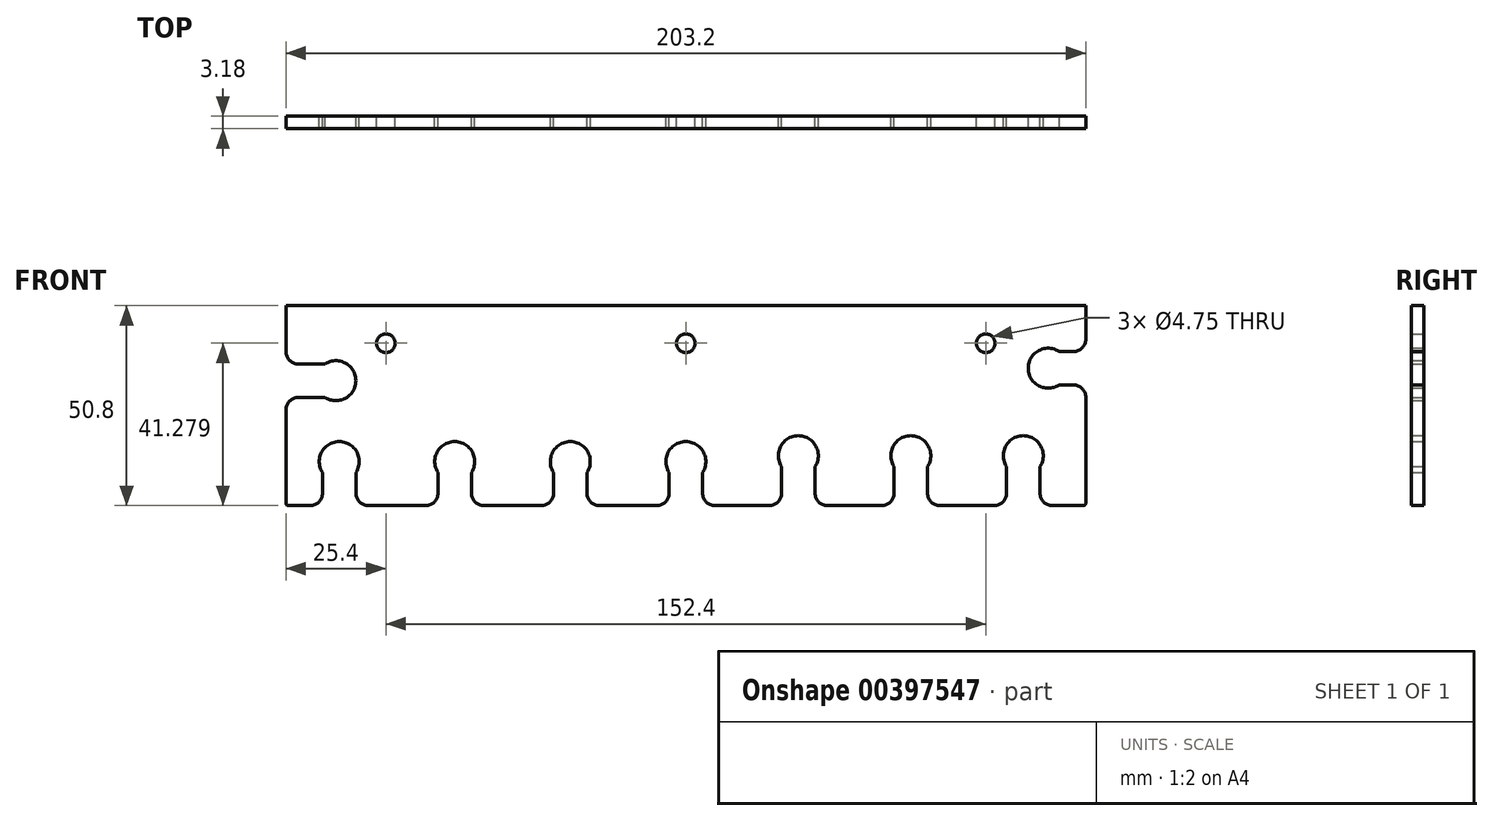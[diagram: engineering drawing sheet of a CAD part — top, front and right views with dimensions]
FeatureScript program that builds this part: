
annotation { "Feature Type Name" : "Feature", "Feature Type Description" : "" }
export const myFeature = defineFeature(function(context is Context, id is Id, definition is map)
    precondition{}
    {
        {
            var Q0;
            Q0=qCreatedBy(makeId("Front.planeOp"),FACE);
            var sketch = newSketch(context, id + "F0", { "sketchPlane" : qUnion([Q0])});
            skLineSegment(sketch, "E0.bottom", {"start": v(76.2, 26.88) * mm, "end": v(-101.6, 26.88) * mm});
            skLineSegment(sketch, "E0.top", {"start": v(100.97, -23.92) * mm, "end": v(93.14, -23.92) * mm});
            skLineSegment(sketch, "E0.left", {"start": v(101.6, 26.88) * mm, "end": v(101.6, 18.43) * mm});
            skLineSegment(sketch, "E0.right", {"start": v(-101.6, 26.88) * mm, "end": v(-101.6, 15.25) * mm});
            skPoint(sketch, "E1.endSnap0", {"position": v(0, -23.92) * mm});
            skArc(sketch, "E2", {"start": v(4.24, -15.5) * mm, "mid": v(0, -7.62) * mm, "end": v(-4.24, -15.5) * mm});
            skLineSegment(sketch, "E3", {"start": v(-4.24, -20.74) * mm, "end": v(-4.24, -15.5) * mm});
            skLineSegment(sketch, "E4", {"start": v(4.24, -20.74) * mm, "end": v(4.24, -15.5) * mm});
            skLineSegment(sketch, "E5.1.0.0", {"start": v(24.33, -20.74) * mm, "end": v(24.33, -14.01) * mm});
            skArc(sketch, "E5.1.0.1", {"start": v(32.82, -14.01) * mm, "mid": v(28.58, -6.14) * mm, "end": v(24.33, -14.01) * mm});
            skLineSegment(sketch, "E5.1.0.2", {"start": v(32.82, -20.74) * mm, "end": v(32.82, -14.01) * mm});
            skLineSegment(sketch, "E5.2.0.0", {"start": v(52.9, -20.74) * mm, "end": v(52.9, -14.01) * mm});
            skArc(sketch, "E5.2.0.1", {"start": v(61.4, -14.01) * mm, "mid": v(57.15, -6.14) * mm, "end": v(52.9, -14.01) * mm});
            skLineSegment(sketch, "E5.2.0.2", {"start": v(61.4, -20.74) * mm, "end": v(61.4, -14.01) * mm});
            skLineSegment(sketch, "E5.3.0.0", {"start": v(81.48, -20.74) * mm, "end": v(81.48, -14.01) * mm});
            skArc(sketch, "E5.3.0.1", {"start": v(89.97, -14.01) * mm, "mid": v(85.73, -6.14) * mm, "end": v(81.48, -14.01) * mm});
            skLineSegment(sketch, "E5.3.0.2", {"start": v(89.97, -20.74) * mm, "end": v(89.97, -14.01) * mm});
            skLineSegment(sketch, "E6.1.0.0", {"start": v(-25.11, -20.74) * mm, "end": v(-25.11, -15.5) * mm});
            skArc(sketch, "E6.1.0.1", {"start": v(-25.11, -15.5) * mm, "mid": v(-29.35, -7.62) * mm, "end": v(-33.6, -15.5) * mm});
            skLineSegment(sketch, "E6.1.0.2", {"start": v(-33.6, -20.74) * mm, "end": v(-33.6, -15.5) * mm});
            skLineSegment(sketch, "E6.2.0.0", {"start": v(-54.47, -20.74) * mm, "end": v(-54.47, -15.5) * mm});
            skArc(sketch, "E6.2.0.1", {"start": v(-54.47, -15.5) * mm, "mid": v(-58.7, -7.62) * mm, "end": v(-62.95, -15.5) * mm});
            skLineSegment(sketch, "E6.2.0.2", {"start": v(-62.95, -20.74) * mm, "end": v(-62.95, -15.5) * mm});
            skLineSegment(sketch, "E6.3.0.0", {"start": v(-83.82, -20.74) * mm, "end": v(-83.82, -15.5) * mm});
            skArc(sketch, "E6.3.0.1", {"start": v(-83.82, -15.5) * mm, "mid": v(-88.06, -7.62) * mm, "end": v(-92.3, -15.5) * mm});
            skLineSegment(sketch, "E6.3.0.2", {"start": v(-92.3, -20.74) * mm, "end": v(-92.3, -15.5) * mm});
            skLineSegment(sketch, "E6.direction1", {"start": v(-7.42, -23.92) * mm, "end": v(-21.94, -23.92) * mm, "construction": true});
            skLineSegment(sketch, "E7.trimOffspring", {"start": v(-95.48, -23.92) * mm, "end": v(-100.97, -23.92) * mm});
            skLineSegment(sketch, "E8.trimOffspring", {"start": v(-66.12, -23.92) * mm, "end": v(-80.65, -23.92) * mm});
            skLineSegment(sketch, "E9.trimOffspring", {"start": v(7.42, -23.92) * mm, "end": v(21.16, -23.92) * mm, "construction": true});
            skLineSegment(sketch, "E10.trimOffspring", {"start": v(-4.24, -23.92) * mm, "end": v(-25.11, -23.92) * mm});
            skLineSegment(sketch, "E11.trimOffspring", {"start": v(-36.77, -23.92) * mm, "end": v(-51.3, -23.92) * mm});
            skLineSegment(sketch, "E12.trimOffspring", {"start": v(24.33, -23.92) * mm, "end": v(4.24, -23.92) * mm});
            skLineSegment(sketch, "E13.trimOffspring", {"start": v(49.73, -23.92) * mm, "end": v(36, -23.92) * mm});
            skLineSegment(sketch, "E14.trimOffspring", {"start": v(78.3, -23.92) * mm, "end": v(64.57, -23.92) * mm});
            skArc(sketch, "E15", {"start": v(94.87, 15.25) * mm, "mid": v(87, 11) * mm, "end": v(94.87, 6.77) * mm});
            skLineSegment(sketch, "E16", {"start": v(-101.6, -23.92) * mm, "end": v(-101.6, 3.6) * mm});
            skArc(sketch, "E17", {"start": v(-91.7, 3.6) * mm, "mid": v(-83.82, 7.83) * mm, "end": v(-91.7, 12.08) * mm});
            skLineSegment(sketch, "E18", {"start": v(-98.43, 12.08) * mm, "end": v(-91.7, 12.08) * mm});
            skLineSegment(sketch, "E19", {"start": v(-98.43, 3.6) * mm, "end": v(-91.7, 3.6) * mm});
            skLineSegment(sketch, "E20.trimOffspring", {"start": v(-101.6, 0.42) * mm, "end": v(-101.6, -23.28) * mm});
            skLineSegment(sketch, "E21", {"start": v(98.42, 15.25) * mm, "end": v(94.87, 15.25) * mm});
            skLineSegment(sketch, "E22", {"start": v(98.43, 6.77) * mm, "end": v(94.87, 6.77) * mm});
            skLineSegment(sketch, "E23.trimOffspring", {"start": v(101.6, 3.6) * mm, "end": v(101.6, -23.28) * mm});
            skPoint(sketch, "E24.visualSharp", {"position": v(101.6, 15.25) * mm});
            skArc(sketch, "E24.filletArc", {"start": v(98.42, 15.25) * mm, "mid": v(100.67, 16.18) * mm, "end": v(101.6, 18.43) * mm});
            skPoint(sketch, "E25.visualSharp", {"position": v(101.6, 6.77) * mm});
            skArc(sketch, "E25.filletArc", {"start": v(101.6, 3.6) * mm, "mid": v(100.67, 5.84) * mm, "end": v(98.43, 6.77) * mm});
            skPoint(sketch, "E26.visualSharp", {"position": v(89.97, -23.92) * mm});
            skArc(sketch, "E26.filletArc", {"start": v(89.97, -20.74) * mm, "mid": v(90.9, -22.99) * mm, "end": v(93.14, -23.92) * mm});
            skPoint(sketch, "E27.visualSharp", {"position": v(81.48, -23.92) * mm});
            skArc(sketch, "E27.filletArc", {"start": v(78.3, -23.92) * mm, "mid": v(80.55, -22.99) * mm, "end": v(81.48, -20.74) * mm});
            skPoint(sketch, "E28.visualSharp", {"position": v(61.4, -23.92) * mm});
            skArc(sketch, "E28.filletArc", {"start": v(61.4, -20.74) * mm, "mid": v(62.32, -22.99) * mm, "end": v(64.57, -23.92) * mm});
            skPoint(sketch, "E29.visualSharp", {"position": v(52.9, -23.92) * mm});
            skArc(sketch, "E29.filletArc", {"start": v(49.73, -23.92) * mm, "mid": v(51.98, -22.99) * mm, "end": v(52.9, -20.74) * mm});
            skPoint(sketch, "E30.visualSharp", {"position": v(32.82, -23.92) * mm});
            skArc(sketch, "E30.filletArc", {"start": v(32.82, -20.74) * mm, "mid": v(33.75, -22.99) * mm, "end": v(36, -23.92) * mm});
            skPoint(sketch, "E31.visualSharp", {"position": v(24.33, -23.92) * mm});
            skArc(sketch, "E31.filletArc", {"start": v(21.16, -23.92) * mm, "mid": v(23.4, -22.99) * mm, "end": v(24.33, -20.74) * mm});
            skPoint(sketch, "E32.visualSharp", {"position": v(4.24, -23.92) * mm});
            skArc(sketch, "E32.filletArc", {"start": v(4.24, -20.74) * mm, "mid": v(5.17, -22.99) * mm, "end": v(7.42, -23.92) * mm});
            skPoint(sketch, "E33.visualSharp", {"position": v(-4.24, -23.92) * mm});
            skArc(sketch, "E33.filletArc", {"start": v(-7.42, -23.92) * mm, "mid": v(-5.17, -22.99) * mm, "end": v(-4.24, -20.74) * mm});
            skPoint(sketch, "E34.visualSharp", {"position": v(-25.11, -23.92) * mm});
            skArc(sketch, "E34.filletArc", {"start": v(-25.11, -20.74) * mm, "mid": v(-24.18, -22.99) * mm, "end": v(-21.94, -23.92) * mm});
            skPoint(sketch, "E35.visualSharp", {"position": v(-54.47, -23.92) * mm});
            skArc(sketch, "E35.filletArc", {"start": v(-54.47, -20.74) * mm, "mid": v(-53.54, -22.99) * mm, "end": v(-51.3, -23.92) * mm});
            skPoint(sketch, "E36.visualSharp", {"position": v(-33.6, -23.92) * mm});
            skArc(sketch, "E36.filletArc", {"start": v(-36.77, -23.92) * mm, "mid": v(-34.53, -22.99) * mm, "end": v(-33.6, -20.74) * mm});
            skPoint(sketch, "E37.visualSharp", {"position": v(-62.95, -23.92) * mm});
            skArc(sketch, "E37.filletArc", {"start": v(-66.12, -23.92) * mm, "mid": v(-63.88, -22.99) * mm, "end": v(-62.95, -20.74) * mm});
            skPoint(sketch, "E38.visualSharp", {"position": v(-83.82, -23.92) * mm});
            skArc(sketch, "E38.filletArc", {"start": v(-83.82, -20.74) * mm, "mid": v(-82.9, -22.99) * mm, "end": v(-80.65, -23.92) * mm});
            skPoint(sketch, "E39.visualSharp", {"position": v(-92.3, -23.92) * mm});
            skArc(sketch, "E39.filletArc", {"start": v(-95.48, -23.92) * mm, "mid": v(-93.23, -22.99) * mm, "end": v(-92.3, -20.74) * mm});
            skPoint(sketch, "E40.visualSharp", {"position": v(-101.6, 12.08) * mm});
            skArc(sketch, "E40.filletArc", {"start": v(-101.6, 15.25) * mm, "mid": v(-100.67, 13) * mm, "end": v(-98.43, 12.08) * mm});
            skPoint(sketch, "E41.visualSharp", {"position": v(-101.6, 3.6) * mm});
            skArc(sketch, "E41.filletArc", {"start": v(-98.43, 3.6) * mm, "mid": v(-100.67, 2.66) * mm, "end": v(-101.6, 0.42) * mm});
            skPoint(sketch, "E42.endSnap0", {"position": v(0, 26.88) * mm});
            skLineSegment(sketch, "E43", {"start": v(101.6, 26.88) * mm, "end": v(76.2, 26.88) * mm});
            skCircle(sketch, "E44", {"center": v(-76.2, 17.36) * mm, "radius": 2.37 * mm});
            skCircle(sketch, "E45", {"center": v(0, 17.36) * mm, "radius": 2.37 * mm});
            skCircle(sketch, "E46", {"center": v(76.2, 17.36) * mm, "radius": 2.37 * mm});
            skPoint(sketch, "E47.visualSharp", {"position": v(101.6, -23.92) * mm});
            skArc(sketch, "E47.filletArc", {"start": v(100.97, -23.92) * mm, "mid": v(101.41, -23.73) * mm, "end": v(101.6, -23.28) * mm});
            skPoint(sketch, "E48.visualSharp", {"position": v(-101.6, -23.92) * mm});
            skArc(sketch, "E48.filletArc", {"start": v(-101.6, -23.28) * mm, "mid": v(-101.41, -23.73) * mm, "end": v(-100.97, -23.92) * mm});
            skSolve(sketch);
        }
        {
            var Q0;
            Q0=makeQuery(id+"F0.imprint","IMPRINT",FACE,{"disambiguationData":[TD([[makeQuery(id+"F0.imprint","IMPRINT",EDGE,{"derivedFrom":sQuery(id+"F0.wireOp",EDGE,"E0.bottom")}),1.0]])]});
            extrude(context, id + "F1", {"entities" : qUnion([Q0]), "depth" : 3.17 * mm});
        }
    });
